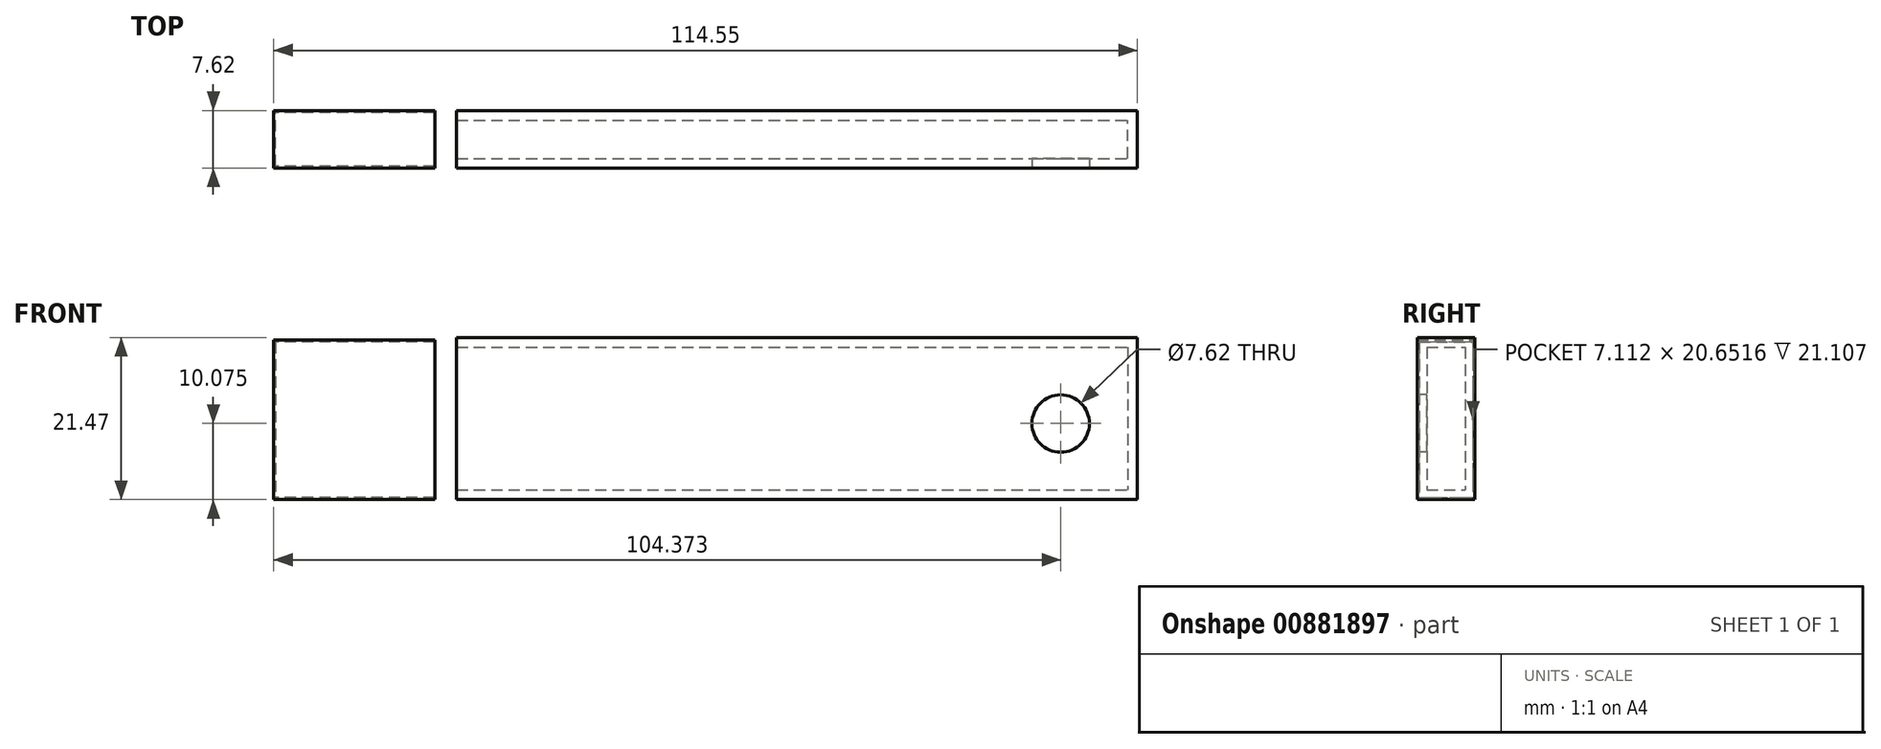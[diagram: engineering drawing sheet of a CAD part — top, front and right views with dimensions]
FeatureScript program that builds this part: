
annotation { "Feature Type Name" : "Feature", "Feature Type Description" : "" }
export const myFeature = defineFeature(function(context is Context, id is Id, definition is map)
    precondition{}
    {
        {
            var Q0;
            Q0=qCreatedBy(makeId("Front.planeOp"),FACE);
            var sketch = newSketch(context, id + "F0", { "sketchPlane" : qUnion([Q0])});
            skLineSegment(sketch, "E0.bottom", {"start": v(-30.56, 21.47) * mm, "end": v(59.75, 21.47) * mm});
            skLineSegment(sketch, "E0.top", {"start": v(-30.56, 0) * mm, "end": v(59.75, 0) * mm});
            skLineSegment(sketch, "E0.left", {"start": v(-30.56, 21.47) * mm, "end": v(-30.56, 0) * mm});
            skLineSegment(sketch, "E0.right", {"start": v(59.75, 21.47) * mm, "end": v(59.75, 0) * mm});
            skSolve(sketch);
        }
        {
            var Q0;
            Q0 = qSketchRegion(id + "F0", true);
            extrude(context, id + "F1", {"entities" : qUnion([Q0]), "depth" : 7.62 * mm, "offsetDistance" : 25.4 * mm});
        }
        {
            var Q0;
            Q0=makeQuery(id+"F1.opExtrude","SWEPT_FACE",FACE,{"disambiguationData":[OSD([sQuery(id+"F0.wireOp",EDGE,"E0.left")])]});
            shell(context, id + "F2", {"entities" : qUnion([Q0]), "thickness" : 1.27 * mm});
        }
        {
            var Q0;
            Q0=makeQuery(id+"F1.opExtrude","CAP_FACE",FACE,{"disambiguationData":[OSD([sQuery(id+"F0.wireOp",EDGE,"E0.bottom"),sQuery(id+"F0.wireOp",EDGE,"E0.top"),sQuery(id+"F0.wireOp",EDGE,"E0.left"),sQuery(id+"F0.wireOp",EDGE,"E0.right")])],"isStart":false});
            var sketch = newSketch(context, id + "F3", { "sketchPlane" : qUnion([Q0])});
            skSolve(sketch);
        }
        {
            var Q0;
            Q0=makeQuery(id+"F3.imprint","IMPRINT",FACE,{"disambiguationData":[TD([[makeQuery(id+"F3.imprint","IMPRINT",EDGE,{"derivedFrom":makeQuery(id+"F1.opExtrude","CAP_EDGE",EDGE,{"disambiguationData":[OSD([sQuery(id+"F0.wireOp",EDGE,"E0.bottom")])],"isStart":false})}),-1.0]])]});
            var sketch = newSketch(context, id + "F4", { "sketchPlane" : qUnion([Q0])});
            skCircle(sketch, "E1", {"center": v(49.57, 10.08) * mm, "radius": 3.63 * mm});
            skSolve(sketch);
        }
        {
            var Q0;
            Q0=sQuery(id+"F4.wireOp",VERTEX,"E1.center");
            var Q1;
            Q1=makeQuery(id+"F1.opExtrude","SWEPT_BODY",BODY,{"disambiguationData":[OSD([sQuery(id+"F0.wireOp",EDGE,"E0.bottom"),sQuery(id+"F0.wireOp",EDGE,"E0.top"),sQuery(id+"F0.wireOp",EDGE,"E0.left"),sQuery(id+"F0.wireOp",EDGE,"E0.right")])]});
            hole(context, id + "F5", {"style" : HoleStyle.SIMPLE, "endStyle" : HoleEndStyle.BLIND, "holeDiameter" : 7.62 * mm, "majorDiameter" : 6.35 * mm, "holeDepth" : 2.54 * mm, "isTappedThrough" : true, "tappedDepth" : 12.7 * mm, "tapClearance" : 3, "startFromSketch" : true, "locations" : qUnion([Q0]), "scope" : qUnion([Q1])});
        }
        {
            var Q0;
            Q0=qCreatedBy(makeId("Front.planeOp"),FACE);
            var sketch = newSketch(context, id + "F6", { "sketchPlane" : qUnion([Q0])});
            skLineSegment(sketch, "E2.bottom", {"start": v(-33.44, 21.16) * mm, "end": v(-54.8, 21.16) * mm});
            skLineSegment(sketch, "E2.top", {"start": v(-33.44, 0) * mm, "end": v(-54.8, 0) * mm});
            skLineSegment(sketch, "E2.left", {"start": v(-33.44, 21.16) * mm, "end": v(-33.44, 0) * mm});
            skLineSegment(sketch, "E2.right", {"start": v(-54.8, 21.16) * mm, "end": v(-54.8, 0) * mm});
            skSolve(sketch);
        }
        {
            var Q0;
            Q0=makeQuery(id+"F6.imprint","IMPRINT",FACE,{"disambiguationData":[TD([[makeQuery(id+"F6.imprint","IMPRINT",EDGE,{"derivedFrom":sQuery(id+"F6.wireOp",EDGE,"E2.bottom")}),1.0]])]});
            extrude(context, id + "F7", {"entities" : qUnion([Q0]), "depth" : 7.62 * mm, "offsetDistance" : 25.4 * mm});
        }
        {
            var Q0;
            Q0=makeQuery(id+"F7.opExtrude","SWEPT_FACE",FACE,{"disambiguationData":[OSD([sQuery(id+"F6.wireOp",EDGE,"E2.left")])]});
            shell(context, id + "F8", {"entities" : qUnion([Q0]), "thickness" : 0.25 * mm});
        }
    });
